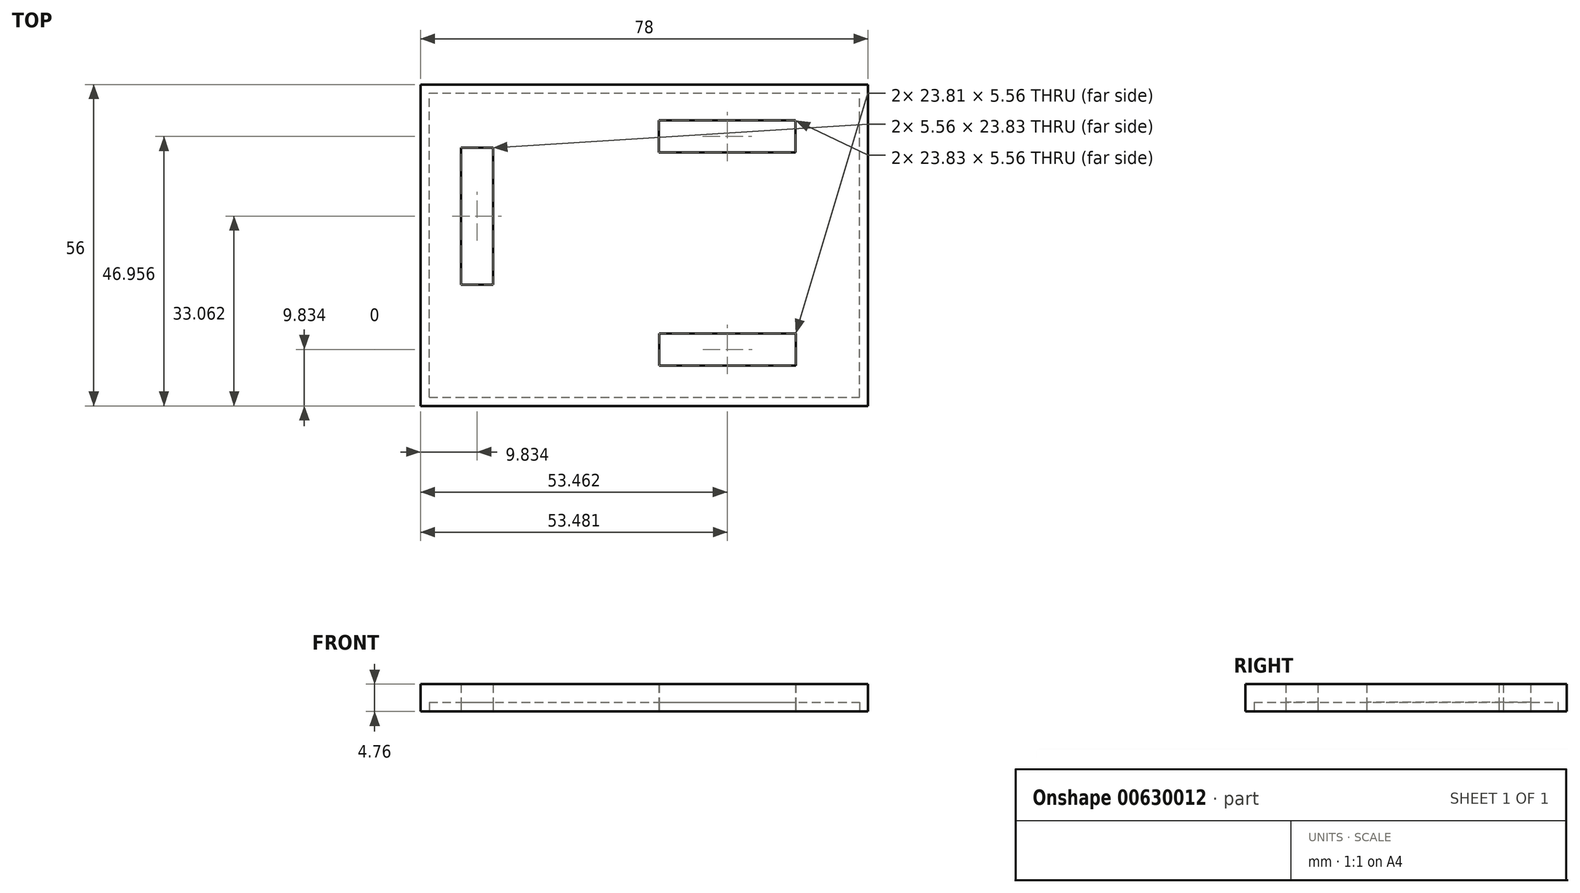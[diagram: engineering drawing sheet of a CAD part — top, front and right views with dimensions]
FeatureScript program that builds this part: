
annotation { "Feature Type Name" : "Feature", "Feature Type Description" : "" }
export const myFeature = defineFeature(function(context is Context, id is Id, definition is map)
    precondition{}
    {
        {
            var Q0;
            Q0=qCreatedBy(makeId("Top.planeOp"),FACE);
            var sketch = newSketch(context, id + "F0", { "sketchPlane" : qUnion([Q0])});
            skLineSegment(sketch, "E0.bottom", {"start": v(-39, 28) * mm, "end": v(39, 28) * mm});
            skLineSegment(sketch, "E0.top", {"start": v(-39, -28) * mm, "end": v(39, -28) * mm});
            skLineSegment(sketch, "E0.left", {"start": v(-39, 28) * mm, "end": v(-39, -28) * mm});
            skLineSegment(sketch, "E0.right", {"start": v(39, 28) * mm, "end": v(39, -28) * mm});
            skPoint(sketch, "E0.middle", {"position": v(0, 0) * mm});
            skLineSegment(sketch, "E1.bottom", {"start": v(-37.5, -26.5) * mm, "end": v(37.5, -26.5) * mm});
            skLineSegment(sketch, "E1.top", {"start": v(-37.5, 26.5) * mm, "end": v(37.5, 26.5) * mm});
            skLineSegment(sketch, "E1.left", {"start": v(-37.5, -26.5) * mm, "end": v(-37.5, 26.5) * mm});
            skLineSegment(sketch, "E1.right", {"start": v(37.5, -26.5) * mm, "end": v(37.5, 26.5) * mm});
            skLineSegment(sketch, "E2.bottom", {"start": v(2.58, -15.39) * mm, "end": v(26.39, -15.39) * mm});
            skLineSegment(sketch, "E2.top", {"start": v(2.58, -20.94) * mm, "end": v(26.39, -20.94) * mm});
            skLineSegment(sketch, "E2.left", {"start": v(2.58, -15.39) * mm, "end": v(2.58, -20.94) * mm});
            skLineSegment(sketch, "E2.right", {"start": v(26.39, -15.39) * mm, "end": v(26.39, -20.94) * mm});
            skLineSegment(sketch, "E3.bottom", {"start": v(-31.94, 16.98) * mm, "end": v(-26.39, 16.98) * mm});
            skLineSegment(sketch, "E3.top", {"start": v(-31.94, -6.85) * mm, "end": v(-26.39, -6.85) * mm});
            skLineSegment(sketch, "E3.left", {"start": v(-31.94, 16.98) * mm, "end": v(-31.94, -6.85) * mm});
            skLineSegment(sketch, "E3.right", {"start": v(-26.39, 16.98) * mm, "end": v(-26.39, -6.85) * mm});
            skLineSegment(sketch, "E4.bottom", {"start": v(2.55, 21.74) * mm, "end": v(26.37, 21.74) * mm});
            skLineSegment(sketch, "E4.top", {"start": v(2.55, 16.17) * mm, "end": v(26.37, 16.17) * mm});
            skLineSegment(sketch, "E4.left", {"start": v(2.55, 21.74) * mm, "end": v(2.55, 16.17) * mm});
            skLineSegment(sketch, "E4.right", {"start": v(26.37, 21.74) * mm, "end": v(26.37, 16.17) * mm});
            skSolve(sketch);
        }
        {
            var Q0;
            Q0 = qSketchRegion(id + "F0", true);
            var Q1;
            {var subQ4=sQuery(id+"F0.wireOp",EDGE,"E1.bottom");Q1=makeQuery(id+"F0.imprint","IMPRINT",FACE,{"disambiguationData":[TD([[makeQuery(id+"F0.imprint","IMPRINT",EDGE,{"derivedFrom":subQ4}),1.0]])]});}
            extrude(context, id + "F1", {"entities" : qUnion([Q0, Q1]), "depth" : 4.76 * mm, "offsetDistance" : 25.4 * mm});
        }
        {
            var Q0;
            Q0=makeQuery(id+"F0.imprint","IMPRINT",FACE,{"disambiguationData":[TD([[makeQuery(id+"F0.imprint","IMPRINT",EDGE,{"derivedFrom":sQuery(id+"F0.wireOp",EDGE,"907b42f6-a3cd-4886-8d7b-21b9f1cb226a")}),1.0]])]});
            var Q1;
            Q1=makeQuery(id+"F0.imprint","IMPRINT",FACE,{"disambiguationData":[TD([[makeQuery(id+"F0.imprint","IMPRINT",EDGE,{"derivedFrom":sQuery(id+"F0.wireOp",EDGE,"2qT4ulvU-UKE9-dtb2-i5I2-ko5FN206pa3X")}),1.0]])]});
            var Q2;
            {var subQ0=sQuery(id+"F0.wireOp",EDGE,"87c1ca84-8655-4782-815f-071953903866");var subQ1=sQuery(id+"F0.wireOp",EDGE,"E1.left");var subQ2=makeQuery(id+"F0.imprint","INTERSECT",VERTEX,{"disambiguationData":[OD(0.0)],"derivedFrom":[subQ1,subQ0]});Q2=makeQuery(id+"F0.imprint","IMPRINT",FACE,{"disambiguationData":[TD([[makeQuery(id+"F0.imprint","IMPRINT",EDGE,{"disambiguationData":[TD([[subQ2,-1.0]])],"derivedFrom":subQ1}),-1.0]])]});}
            var Q3;
            Q3=makeQuery(id+"F0.imprint","IMPRINT",FACE,{"disambiguationData":[TD([[makeQuery(id+"F0.imprint","IMPRINT",EDGE,{"derivedFrom":sQuery(id+"F0.wireOp",EDGE,"7e4b3655-d419-4b39-9dfa-3614d8393ec7")}),1.0]])]});
            var Q4;
            Q4=sQuery(id+"F0.wireOp",EDGE,"907b42f6-a3cd-4886-8d7b-21b9f1cb226a");
            var Q5;
            Q5=sQuery(id+"F0.wireOp",EDGE,"2qT4ulvU-UKE9-dtb2-i5I2-ko5FN206pa3X");
            var Q6;
            Q6=sQuery(id+"F0.wireOp",EDGE,"87c1ca84-8655-4782-815f-071953903866");
            var Q7;
            Q7=sQuery(id+"F0.wireOp",EDGE,"7e4b3655-d419-4b39-9dfa-3614d8393ec7");
            extrude(context, id + "F2", {"entities" : qUnion([Q0, Q1, Q2, Q3]), "surfaceEntities" : qUnion([Q4, Q5, Q6, Q7]), "depth" : 1.59 * mm, "offsetDistance" : 25.4 * mm});
        }
        {
            var Q0;
            Q0=makeQuery(id+"F0.imprint","IMPRINT",FACE,{"disambiguationData":[TD([[makeQuery(id+"F0.imprint","IMPRINT",EDGE,{"derivedFrom":sQuery(id+"F0.wireOp",EDGE,"E3.bottom")}),-1.0]])]});
            var Q1;
            Q1=makeQuery(id+"F0.imprint","IMPRINT",FACE,{"disambiguationData":[TD([[makeQuery(id+"F0.imprint","IMPRINT",EDGE,{"derivedFrom":sQuery(id+"F0.wireOp",EDGE,"E4.bottom")}),-1.0]])]});
            var Q2;
            Q2=makeQuery(id+"F0.imprint","IMPRINT",FACE,{"disambiguationData":[TD([[makeQuery(id+"F0.imprint","IMPRINT",EDGE,{"derivedFrom":sQuery(id+"F0.wireOp",EDGE,"E2.bottom")}),-1.0]])]});
            extrude(context, id + "F3", {"entities" : qUnion([Q0, Q1, Q2]), "operationType" : NewBodyOperationType.REMOVE, "oppositeDirection" : true, "depth" : 25.4 * mm, "offsetDistance" : 25.4 * mm});
        }
    });
